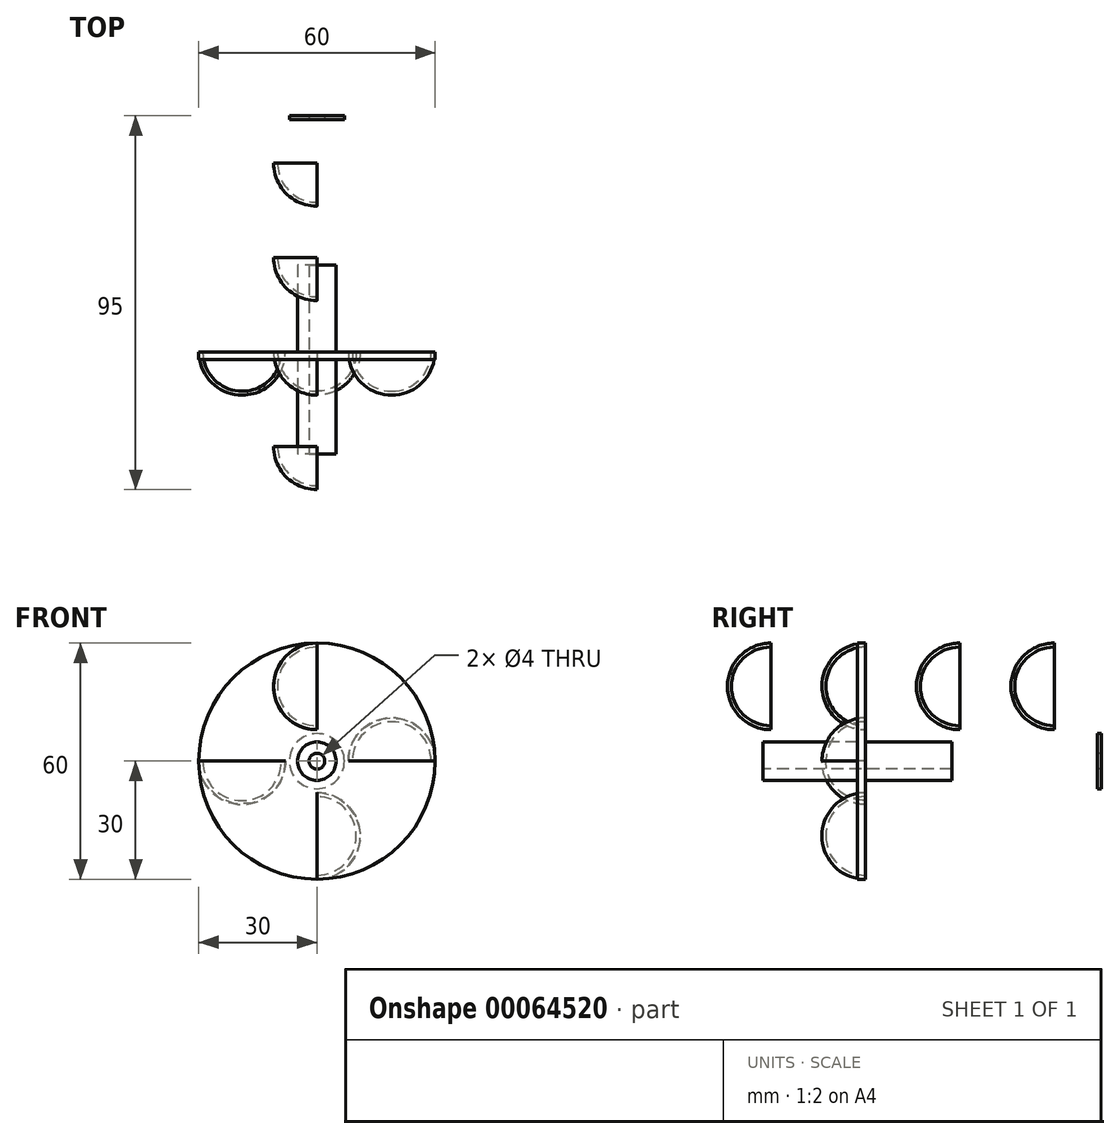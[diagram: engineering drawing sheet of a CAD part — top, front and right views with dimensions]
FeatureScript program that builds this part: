
annotation { "Feature Type Name" : "Feature", "Feature Type Description" : "" }
export const myFeature = defineFeature(function(context is Context, id is Id, definition is map)
    precondition{}
    {
        {
            var Q0;
            Q0=qCreatedBy(makeId("Right.planeOp"),FACE);
            var sketch = newSketch(context, id + "F0", { "sketchPlane" : qUnion([Q0])});
            skArc(sketch, "E0", {"start": v(0, 10) * mm, "mid": v(-7.07, 7.07) * mm, "end": v(-10, 0) * mm});
            skLineSegment(sketch, "E1", {"start": v(-10, 0) * mm, "end": v(0, 0) * mm});
            skLineSegment(sketch, "E2", {"start": v(0, 10) * mm, "end": v(0, 0) * mm});
            skArc(sketch, "E3", {"start": v(0, 11) * mm, "mid": v(-7.78, 7.78) * mm, "end": v(-11, 0) * mm});
            skLineSegment(sketch, "E4", {"start": v(0, 10) * mm, "end": v(0, 11) * mm});
            skLineSegment(sketch, "E5", {"start": v(-11, 0) * mm, "end": v(-10, 0) * mm});
            skSolve(sketch);
        }
        {
            var Q0;
            Q0=makeQuery(id+"F0.imprint","IMPRINT",FACE,{"disambiguationData":[TD([[makeQuery(id+"F0.imprint","IMPRINT",EDGE,{"derivedFrom":sQuery(id+"F0.wireOp",EDGE,"E0")}),-1.0]])]});
            var Q1;
            Q1=sQuery(id+"F0.wireOp",EDGE,"E0");
            var Q2;
            Q2=sQuery(id+"F0.wireOp",EDGE,"E1");
            revolve(context, id + "F1", {"entities" : qUnion([Q0]), "surfaceEntities" : qUnion([Q1]), "axis" : qUnion([Q2]), "revolveType" : RevolveType.TWO_DIRECTIONS, "angle" : 90 * degree, "angleBack" : 270 * degree});
        }
        {
            var Q0;
            Q0=makeQuery(id+"F1.opRevolve","SWEPT_BODY",BODY,{"disambiguationData":[OSD([sQuery(id+"F0.wireOp",EDGE,"E0"),sQuery(id+"F0.wireOp",EDGE,"E3"),sQuery(id+"F0.wireOp",EDGE,"E4"),sQuery(id+"F0.wireOp",EDGE,"E5")])]});
            transform(context, id + "F2", {"entities" : qUnion([Q0]), "transformType" : TransformType.TRANSLATION_3D, "dx" : 19 * mm, "dy" : 0 * mm, "dz" : 0 * mm, "makeCopy" : false});
        }
        {
            var Q0;
            Q0=qCreatedBy(makeId("Right.planeOp"),FACE);
            var sketch = newSketch(context, id + "F3", { "sketchPlane" : qUnion([Q0])});
            skLineSegment(sketch, "E6", {"start": v(-12, 0) * mm, "end": v(0, 0) * mm});
            skLineSegment(sketch, "E7", {"start": v(0, 0) * mm, "end": v(10, 0) * mm});
            skLineSegment(sketch, "E8", {"start": v(0, 0) * mm, "end": v(0, 30) * mm});
            skLineSegment(sketch, "E9.bottom", {"start": v(-2, 0) * mm, "end": v(0, 0) * mm});
            skLineSegment(sketch, "E9.top", {"start": v(-2, 30) * mm, "end": v(0, 30) * mm});
            skLineSegment(sketch, "E9.right", {"start": v(-2, 0) * mm, "end": v(-2, 30) * mm});
            skLineSegment(sketch, "E10", {"start": v(-24, 4.9) * mm, "end": v(0, 4.9) * mm});
            skLineSegment(sketch, "E11", {"start": v(0, 4.9) * mm, "end": v(10, 4.9) * mm});
            skLineSegment(sketch, "E12", {"start": v(-2, 4.9) * mm, "end": v(-2, 0) * mm});
            skLineSegment(sketch, "E13", {"start": v(0, 4.9) * mm, "end": v(0, 0) * mm});
            skLineSegment(sketch, "E14", {"start": v(22, 0) * mm, "end": v(34, 0) * mm});
            skLineSegment(sketch, "E15", {"start": v(34, 0) * mm, "end": v(46, 0) * mm});
            skLineSegment(sketch, "E16", {"start": v(-12, 0) * mm, "end": v(-24, 0) * mm});
            skLineSegment(sketch, "E17", {"start": v(-24, 0) * mm, "end": v(-36, 0) * mm});
            skLineSegment(sketch, "E18", {"start": v(-36, 0) * mm, "end": v(-48, 0) * mm});
            skLineSegment(sketch, "E19", {"start": v(10, 0) * mm, "end": v(22, 0) * mm});
            skLineSegment(sketch, "E20", {"start": v(-24, 4.9) * mm, "end": v(-24, 4.9) * mm});
            skLineSegment(sketch, "E21", {"start": v(10, 4.9) * mm, "end": v(22, 4.9) * mm});
            skLineSegment(sketch, "E22", {"start": v(-24, 4.9) * mm, "end": v(-36, 4.9) * mm});
            skLineSegment(sketch, "E23", {"start": v(-36, 0) * mm, "end": v(-36, 4.9) * mm});
            skLineSegment(sketch, "E24", {"start": v(46, 0) * mm, "end": v(65, 0) * mm});
            skLineSegment(sketch, "E25", {"start": v(65, 0) * mm, "end": v(77, 0) * mm});
            skLineSegment(sketch, "E26", {"start": v(-48, 0) * mm, "end": v(-60, 0) * mm});
            skLineSegment(sketch, "E27", {"start": v(-36, 0) * mm, "end": v(-36, 2) * mm});
            skLineSegment(sketch, "E28", {"start": v(-36, 2) * mm, "end": v(22, 2) * mm});
            skLineSegment(sketch, "E29", {"start": v(-36, 0) * mm, "end": v(-38, 0) * mm});
            skLineSegment(sketch, "E30", {"start": v(10, 4.9) * mm, "end": v(10, 0) * mm});
            skLineSegment(sketch, "E31", {"start": v(10, 0) * mm, "end": v(10, 30) * mm});
            skLineSegment(sketch, "E32", {"start": v(10, 30) * mm, "end": v(12, 30) * mm});
            skLineSegment(sketch, "E33", {"start": v(12, 30) * mm, "end": v(12, 0) * mm});
            skLineSegment(sketch, "E34", {"start": v(22, 0) * mm, "end": v(22, 30) * mm});
            skLineSegment(sketch, "E35", {"start": v(22, 30) * mm, "end": v(24, 30) * mm});
            skLineSegment(sketch, "E36", {"start": v(24, 30) * mm, "end": v(24, 0) * mm});
            skLineSegment(sketch, "E37", {"start": v(34, 0) * mm, "end": v(34, 30) * mm});
            skLineSegment(sketch, "E38", {"start": v(34, 30) * mm, "end": v(36, 30) * mm});
            skLineSegment(sketch, "E39", {"start": v(36, 30) * mm, "end": v(36, 0) * mm});
            skLineSegment(sketch, "E40", {"start": v(46, 0) * mm, "end": v(46, 30) * mm});
            skLineSegment(sketch, "E41", {"start": v(46, 30) * mm, "end": v(48, 30) * mm});
            skLineSegment(sketch, "E42", {"start": v(48, 30) * mm, "end": v(48, 0) * mm});
            skLineSegment(sketch, "E43", {"start": v(22, 4.9) * mm, "end": v(34, 4.9) * mm});
            skLineSegment(sketch, "E44", {"start": v(34, 4.9) * mm, "end": v(46, 4.9) * mm});
            skLineSegment(sketch, "E45", {"start": v(46, 4.9) * mm, "end": v(65, 4.9) * mm});
            skLineSegment(sketch, "E46", {"start": v(65, 4.9) * mm, "end": v(65, 0) * mm});
            skLineSegment(sketch, "E47", {"start": v(22, 2) * mm, "end": v(48, 2) * mm});
            skLineSegment(sketch, "E48", {"start": v(-12, 30) * mm, "end": v(-14, 30) * mm});
            skLineSegment(sketch, "E49", {"start": v(-14, 30) * mm, "end": v(-14, 0) * mm});
            skLineSegment(sketch, "E50", {"start": v(-24, 0) * mm, "end": v(-24, 30) * mm});
            skLineSegment(sketch, "E51", {"start": v(-24, 30) * mm, "end": v(-26, 30) * mm});
            skLineSegment(sketch, "E52", {"start": v(-26, 30) * mm, "end": v(-26, 0) * mm});
            skLineSegment(sketch, "E53", {"start": v(-36, 0) * mm, "end": v(-36, 30) * mm});
            skLineSegment(sketch, "E54", {"start": v(-36, 30) * mm, "end": v(-38, 30) * mm});
            skLineSegment(sketch, "E55", {"start": v(-38, 30) * mm, "end": v(-38, 0) * mm});
            skLineSegment(sketch, "E56", {"start": v(-36, 4.9) * mm, "end": v(-48, 4.9) * mm});
            skLineSegment(sketch, "E57", {"start": v(-48, 4.9) * mm, "end": v(-60, 4.9) * mm});
            skLineSegment(sketch, "E58", {"start": v(-60, 4.9) * mm, "end": v(-60, 0) * mm});
            skLineSegment(sketch, "E59", {"start": v(-36, 2) * mm, "end": v(-60, 2) * mm});
            skLineSegment(sketch, "E60", {"start": v(-60, 0) * mm, "end": v(-60, 2) * mm});
            skLineSegment(sketch, "E61", {"start": v(-2, 4.9) * mm, "end": v(0, 4.9) * mm});
            skLineSegment(sketch, "E62", {"start": v(0, 0) * mm, "end": v(-2, 0) * mm});
            skLineSegment(sketch, "E63", {"start": v(10, 0) * mm, "end": v(-2, 0) * mm});
            skLineSegment(sketch, "E64", {"start": v(10, 4.9) * mm, "end": v(-2, 4.9) * mm});
            skLineSegment(sketch, "E65", {"start": v(22, 2) * mm, "end": v(12, 2) * mm});
            skLineSegment(sketch, "E66", {"start": v(-2, 4.9) * mm, "end": v(10, 4.9) * mm});
            skLineSegment(sketch, "E67", {"start": v(-60, 4.9) * mm, "end": v(-63.18, 4.9) * mm});
            skLineSegment(sketch, "E68", {"start": v(-63.18, 4.9) * mm, "end": v(-63.18, 0) * mm});
            skLineSegment(sketch, "E69", {"start": v(-63.18, 0) * mm, "end": v(-60, 0) * mm});
            skLineSegment(sketch, "E70", {"start": v(-63.18, 0) * mm, "end": v(-63.18, 2) * mm});
            skLineSegment(sketch, "E71", {"start": v(60, 0) * mm, "end": v(60, 7) * mm});
            skLineSegment(sketch, "E72", {"start": v(60, 7) * mm, "end": v(59, 7) * mm});
            skLineSegment(sketch, "E73", {"start": v(59, 0) * mm, "end": v(59, 7) * mm});
            skLineSegment(sketch, "E74", {"start": v(-12, 30) * mm, "end": v(-12, 0) * mm});
            skPoint(sketch, "E75", {"position": v(65, 2) * mm});
            skLineSegment(sketch, "E76", {"start": v(48, 2) * mm, "end": v(65, 2) * mm});
            skLineSegment(sketch, "E77", {"start": v(65, 2) * mm, "end": v(65, 0) * mm});
            skLineSegment(sketch, "E78", {"start": v(-60, 2) * mm, "end": v(-63.18, 2) * mm});
            skLineSegment(sketch, "E79", {"start": v(-60, 0) * mm, "end": v(-38, 0) * mm});
            skLineSegment(sketch, "E80", {"start": v(-60, 4.9) * mm, "end": v(-36, 4.9) * mm});
            skLineSegment(sketch, "E81", {"start": v(-60, 0) * mm, "end": v(-36, 0) * mm});
            skLineSegment(sketch, "E82", {"start": v(-48, 4.9) * mm, "end": v(-48, 0) * mm});
            skSolve(sketch);
        }
        {
            var Q0;
            {var subQ1=sQuery(id+"F3.wireOp",EDGE,"E12");var subQ3=sQuery(id+"F3.wireOp",EDGE,"E28");var subQ4=makeQuery(id+"F3.imprint","INTERSECT",VERTEX,{"derivedFrom":[subQ1,subQ3]});Q0=makeQuery(id+"F3.imprint","IMPRINT",FACE,{"disambiguationData":[TD([[makeQuery(id+"F3.imprint","IMPRINT",EDGE,{"disambiguationData":[TD([[subQ4,-1.0]])],"derivedFrom":subQ3}),1.0]])]});}
            var Q1;
            Q1=makeQuery(id+"F3.imprint","IMPRINT",FACE,{"disambiguationData":[TD([[makeQuery(id+"F3.imprint","IMPRINT",EDGE,{"derivedFrom":sQuery(id+"F3.wireOp",EDGE,"E9.top")}),-1.0]])]});
            var Q2;
            {var subQ0=sQuery(id+"F3.wireOp",EDGE,"E73");var subQ1=sQuery(id+"F3.wireOp",EDGE,"E45");var subQ2=makeQuery(id+"F3.imprint","INTERSECT",VERTEX,{"derivedFrom":[subQ1,subQ0]});Q2=makeQuery(id+"F3.imprint","IMPRINT",FACE,{"disambiguationData":[TD([[makeQuery(id+"F3.imprint","IMPRINT",EDGE,{"disambiguationData":[TD([[subQ2,-1.0]])],"derivedFrom":subQ1}),-1.0]])]});}
            var Q3;
            {var subQ5=sQuery(id+"F3.wireOp",EDGE,"E72");Q3=makeQuery(id+"F3.imprint","IMPRINT",FACE,{"disambiguationData":[TD([[makeQuery(id+"F3.imprint","IMPRINT",EDGE,{"derivedFrom":subQ5}),1.0]])]});}
            var Q4;
            Q4=sQuery(id+"F3.wireOp",EDGE,"E6");
            revolve(context, id + "F4", {"entities" : qUnion([Q0, Q1, Q2, Q3]), "axis" : qUnion([Q4]), "revolveType" : RevolveType.FULL});
        }
        {
            var Q0;
            Q0=makeQuery(id+"F1.opRevolve","SWEPT_BODY",BODY,{"disambiguationData":[OSD([sQuery(id+"F0.wireOp",EDGE,"E0"),sQuery(id+"F0.wireOp",EDGE,"E3"),sQuery(id+"F0.wireOp",EDGE,"E4"),sQuery(id+"F0.wireOp",EDGE,"E5")])]});
            var Q1;
            Q1=sQuery(id+"F3.wireOp",EDGE,"E6");
            transform(context, id + "F5", {"entities" : qUnion([Q0]), "transformType" : TransformType.ROTATION, "transformAxis" : qUnion([Q1]), "angle" : 90 * degree, "makeCopy" : true});
        }
        {
            var Q0;
            Q0=makeQuery(id+"F1.opRevolve","SWEPT_BODY",BODY,{"disambiguationData":[OSD([sQuery(id+"F0.wireOp",EDGE,"E0"),sQuery(id+"F0.wireOp",EDGE,"E3"),sQuery(id+"F0.wireOp",EDGE,"E4"),sQuery(id+"F0.wireOp",EDGE,"E5")])]});
            var Q1;
            Q1=makeQuery(id+"F5.opPattern","COPY",BODY,{"derivedFrom":makeQuery(id+"F1.opRevolve","SWEPT_BODY",BODY,{"disambiguationData":[OSD([sQuery(id+"F0.wireOp",EDGE,"E0"),sQuery(id+"F0.wireOp",EDGE,"E3"),sQuery(id+"F0.wireOp",EDGE,"E4"),sQuery(id+"F0.wireOp",EDGE,"E5")])]}),"instanceName":"1"});
            var Q2;
            Q2=sQuery(id+"F3.wireOp",EDGE,"E7");
            transform(context, id + "F6", {"entities" : qUnion([Q0, Q1]), "transformType" : TransformType.ROTATION, "transformAxis" : qUnion([Q2]), "angle" : 180 * degree, "makeCopy" : true});
        }
        {
            var Q0;
            Q0=makeQuery(id+"F6.opPattern","COPY",BODY,{"derivedFrom":makeQuery(id+"F5.opPattern","COPY",BODY,{"derivedFrom":makeQuery(id+"F1.opRevolve","SWEPT_BODY",BODY,{"disambiguationData":[OSD([sQuery(id+"F0.wireOp",EDGE,"E0"),sQuery(id+"F0.wireOp",EDGE,"E3"),sQuery(id+"F0.wireOp",EDGE,"E4"),sQuery(id+"F0.wireOp",EDGE,"E5")])]}),"instanceName":"1"}),"instanceName":"1"});
            var Q1;
            Q1=sQuery(id+"F3.wireOp",VERTEX,"E8.start");
            var Q2;
            Q2=sQuery(id+"F3.wireOp",VERTEX,"E17.start");
            transform(context, id + "F7", {"entities" : qUnion([Q0]), "transformType" : TransformType.TRANSLATION_ENTITY, "oppositeDirectionEntity" : false, "transformLine" : qUnion([Q1, Q2]), "makeCopy" : true});
        }
        {
            var Q0;
            Q0=makeQuery(id+"F7.opPattern","COPY",BODY,{"derivedFrom":makeQuery(id+"F6.opPattern","COPY",BODY,{"derivedFrom":makeQuery(id+"F5.opPattern","COPY",BODY,{"derivedFrom":makeQuery(id+"F1.opRevolve","SWEPT_BODY",BODY,{"disambiguationData":[OSD([sQuery(id+"F0.wireOp",EDGE,"E0"),sQuery(id+"F0.wireOp",EDGE,"E3"),sQuery(id+"F0.wireOp",EDGE,"E4"),sQuery(id+"F0.wireOp",EDGE,"E5")])]}),"instanceName":"1"}),"instanceName":"1"}),"instanceName":"1"});
            var Q1;
            Q1=makeQuery(id+"F6.opPattern","COPY",BODY,{"derivedFrom":makeQuery(id+"F5.opPattern","COPY",BODY,{"derivedFrom":makeQuery(id+"F1.opRevolve","SWEPT_BODY",BODY,{"disambiguationData":[OSD([sQuery(id+"F0.wireOp",EDGE,"E0"),sQuery(id+"F0.wireOp",EDGE,"E3"),sQuery(id+"F0.wireOp",EDGE,"E4"),sQuery(id+"F0.wireOp",EDGE,"E5")])]}),"instanceName":"1"}),"instanceName":"1"});
            var Q2;
            Q2=sQuery(id+"F3.wireOp",VERTEX,"E8.start");
            var Q3;
            Q3=sQuery(id+"F3.wireOp",VERTEX,"E42.end");
            transform(context, id + "F8", {"entities" : qUnion([Q0, Q1]), "transformType" : TransformType.TRANSLATION_ENTITY, "oppositeDirectionEntity" : false, "transformLine" : qUnion([Q2, Q3]), "makeCopy" : true});
        }
    });
